# Revit family: Ballorex Venturi FODRV с дренажем
name_source: partatom
category: Арматура трубопроводов
revit_build: Autodesk Revit 2017 (Build: 20171027_0315(x64)
units: mm (PartAtom-declared; Revit-internal decimal feet)

## family parameters
Всегда вертикально = Да
На основе рабочей плоскости = Нет
Общий = Нет
При загрузке вырезать с полостями = Нет
Размер круглого соединителя = Использовать радиус
Тип детали = Вставляется

## types (11) — shared parameters
ADSK_Единица измерения = шт
ADSK_Завод-изготовитель = Meibes
ADSK_Наименование = Клапан балансировочный Ballorex Venturi FODRV с дренажем
URL = www.meibes.ru/
l = 15 мм
Группа модели = Клапан балансировочный Ballorex Venturi FODRV с дренажем
Изготовитель = Meibes
Материал полимера = Фильтр_Черный
Материал фитинга = Фильтр_Латунь
Разработчик = ООО ПРОРУБИМ
Разработчик (телефон) = +7(495)649-85-43
Разработчик модели (URL) = http://prorubim.com

## per-type parameters (varying)
| type | ADSK_Код изделия | ADSK_Обозначение | D2 | DN | DN+t | H | L | L1 | L2 | L3 | R | R3 | S | l3 | l3-1 | l4 | l4-1 |
| 50H | ME 80597.541 | DN50H | 35 мм | 50 мм | 56 мм | 120 мм | 156 мм | 122 мм | 221 мм | 238 мм | 25 мм | 15 мм | 66 мм | 62 мм | 10 мм | 94 мм | 16 мм |
| 40H | ME 80597.540 | DN40H | 28 мм | 40 мм | 46 мм | 113 мм | 140 мм | 122 мм | 213 мм | 234 мм | 20 мм | 13 мм | 56 мм | 56 мм | 9 мм | 84 мм | 14 мм |
| 32H | ME 80597.539 | DN32H | 22 мм | 32 мм | 38 мм | 109 мм | 130 мм | 122 мм | 208 мм | 228 мм | 16 мм | 11 мм | 48 мм | 52 мм | 9 мм | 78 мм | 13 мм |
| 25H | ME 80597.538 | DN25H | 18 мм | 25 мм | 31 мм | 83 мм | 112 мм | 75 мм | 150 мм | 175 мм | 13 мм | 9 мм | 41 мм | 45 мм | 7 мм | 67 мм | 11 мм |
| 25S | ME 80597.537 | DN25S | 18 мм | 25 мм | 31 мм | 83 мм | 112 мм | 75 мм | 150 мм | 175 мм | 13 мм | 9 мм | 41 мм | 45 мм | 7 мм | 67 мм | 11 мм |
| 20H | ME 80597.536 | DN20H | 14 мм | 20 мм | 26 мм | 79 мм | 100 мм | 75 мм | 144 мм | 174 мм | 10 мм | 8 мм | 36 мм | 40 мм | 7 мм | 60 мм | 10 мм |
| 20S | ME 80597.535 | DN20S | 14 мм | 20 мм | 26 мм | 79 мм | 100 мм | 75 мм | 144 мм | 174 мм | 10 мм | 8 мм | 36 мм | 40 мм | 7 мм | 60 мм | 10 мм |
| 20L | ME 80597.534 | DN20L | 14 мм | 20 мм | 26 мм | 79 мм | 100 мм | 75 мм | 144 мм | 174 мм | 10 мм | 8 мм | 36 мм | 40 мм | 7 мм | 60 мм | 10 мм |
| 15H | ME 80597.533 | DN15H | 11 мм | 15 мм | 21 мм | 76 мм | 94 мм | 75 мм | 140 мм | 174 мм | 8 мм | 7 мм | 31 мм | 38 мм | 6 мм | 56 мм | 9 мм |
| 15S | ME 80597.532 | DN15S | 11 мм | 15 мм | 21 мм | 76 мм | 94 мм | 75 мм | 140 мм | 174 мм | 8 мм | 7 мм | 31 мм | 38 мм | 6 мм | 56 мм | 9 мм |
| 15L | ME 80597.531 | DN15L | 11 мм | 15 мм | 21 мм | 76 мм | 94 мм | 75 мм | 140 мм | 174 мм | 8 мм | 7 мм | 31 мм | 38 мм | 6 мм | 56 мм | 9 мм |
